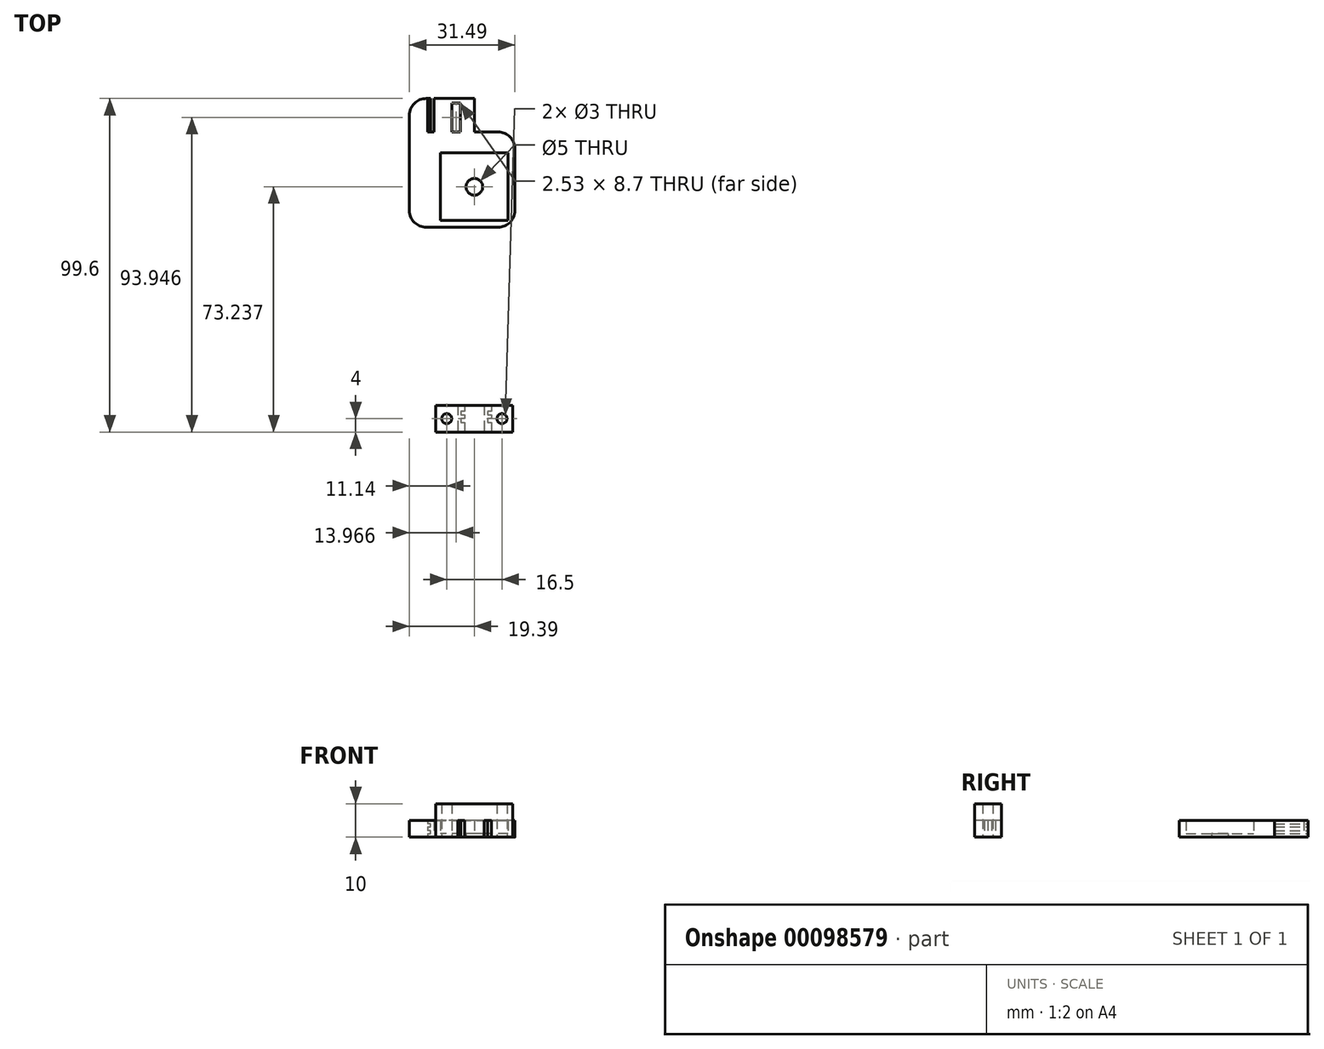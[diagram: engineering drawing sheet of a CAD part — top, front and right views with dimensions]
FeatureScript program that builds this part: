
annotation { "Feature Type Name" : "Feature", "Feature Type Description" : "" }
export const myFeature = defineFeature(function(context is Context, id is Id, definition is map)
    precondition{}
    {
        {
            var Q0;
            Q0=qCreatedBy(makeId("Top.planeOp"),FACE);
            var sketch = newSketch(context, id + "F0", { "sketchPlane" : qUnion([Q0])});
            skLineSegment(sketch, "E0.bottom", {"start": v(-11.5, 4) * mm, "end": v(11.5, 4) * mm});
            skLineSegment(sketch, "E0.top", {"start": v(-11.5, -4) * mm, "end": v(11.5, -4) * mm});
            skLineSegment(sketch, "E0.left", {"start": v(-11.5, 4) * mm, "end": v(-11.5, -4) * mm});
            skLineSegment(sketch, "E0.right", {"start": v(11.5, 4) * mm, "end": v(11.5, -4) * mm});
            skPoint(sketch, "E0.middle", {"position": v(0, 0) * mm});
            skLineSegment(sketch, "E1", {"start": v(-5, 4) * mm, "end": v(-5, -4) * mm});
            skLineSegment(sketch, "E2", {"start": v(-2.9, 4) * mm, "end": v(-2.9, 2.2) * mm});
            skLineSegment(sketch, "E3", {"start": v(-2.9, 2.2) * mm, "end": v(-4, 2.2) * mm});
            skLineSegment(sketch, "E4", {"start": v(-4, 2.2) * mm, "end": v(-4, 1.1) * mm});
            skLineSegment(sketch, "E5", {"start": v(-4, 1.1) * mm, "end": v(-2.9, 1.1) * mm});
            skLineSegment(sketch, "E6", {"start": v(-2.9, 1.1) * mm, "end": v(-2.9, 0) * mm});
            skLineSegment(sketch, "E7", {"start": v(-2.9, 0) * mm, "end": v(-4, 0) * mm});
            skLineSegment(sketch, "E8", {"start": v(-4, 0) * mm, "end": v(-4, -1.1) * mm});
            skLineSegment(sketch, "E9", {"start": v(-4, -1.1) * mm, "end": v(-2.9, -1.1) * mm});
            skLineSegment(sketch, "E10", {"start": v(-2.9, -1.1) * mm, "end": v(-2.9, -4) * mm});
            skLineSegment(sketch, "E11.1.0.0", {"start": v(5.1, 4) * mm, "end": v(5.1, 2.2) * mm});
            skLineSegment(sketch, "E11.1.0.1", {"start": v(5.1, 2.2) * mm, "end": v(4, 2.2) * mm});
            skLineSegment(sketch, "E11.1.0.2", {"start": v(4, 2.2) * mm, "end": v(4, 1.1) * mm});
            skLineSegment(sketch, "E11.1.0.3", {"start": v(4, 1.1) * mm, "end": v(5.1, 1.1) * mm});
            skLineSegment(sketch, "E11.1.0.4", {"start": v(5.1, 1.1) * mm, "end": v(5.1, 0) * mm});
            skLineSegment(sketch, "E11.1.0.5", {"start": v(5.1, 0) * mm, "end": v(4, 0) * mm});
            skLineSegment(sketch, "E11.1.0.6", {"start": v(4, 0) * mm, "end": v(4, -1.1) * mm});
            skLineSegment(sketch, "E11.1.0.7", {"start": v(4, -1.1) * mm, "end": v(5.1, -1.1) * mm});
            skLineSegment(sketch, "E11.1.0.8", {"start": v(5.1, -1.1) * mm, "end": v(5.1, -4) * mm});
            skLineSegment(sketch, "E11.1.0.9", {"start": v(3, 4) * mm, "end": v(3, -4) * mm});
            skLineSegment(sketch, "E11.direction1", {"start": v(-2.9, 2.2) * mm, "end": v(5.1, 2.2) * mm, "construction": true});
            skCircle(sketch, "E12", {"center": v(-8.25, 0) * mm, "radius": 1.5 * mm});
            skLineSegment(sketch, "E13", {"start": v(0, 4) * mm, "end": v(0, -4) * mm, "construction": true});
            skCircle(sketch, "E14.MirrorC", {"center": v(8.25, 0) * mm, "radius": 1.5 * mm});
            skSolve(sketch);
        }
        {
            var Q0;
            {var subQ1=sQuery(id+"F0.wireOp",EDGE,"E0.left");Q0=makeQuery(id+"F0.imprint","IMPRINT",FACE,{"disambiguationData":[TD([[makeQuery(id+"F0.imprint","IMPRINT",EDGE,{"derivedFrom":subQ1}),1.0]])]});}
            var Q1;
            {var subQ0=sQuery(id+"F0.wireOp",EDGE,"E1");Q1=makeQuery(id+"F0.imprint","IMPRINT",FACE,{"disambiguationData":[TD([[makeQuery(id+"F0.imprint","IMPRINT",EDGE,{"derivedFrom":subQ0}),1.0]])]});}
            var Q2;
            {var subQ1=sQuery(id+"F0.wireOp",EDGE,"E11.1.0.0");Q2=makeQuery(id+"F0.imprint","IMPRINT",FACE,{"disambiguationData":[TD([[makeQuery(id+"F0.imprint","IMPRINT",EDGE,{"derivedFrom":subQ1}),-1.0]])]});}
            var Q3;
            {var subQ0=sQuery(id+"F0.wireOp",EDGE,"E0.right");Q3=makeQuery(id+"F0.imprint","IMPRINT",FACE,{"disambiguationData":[TD([[makeQuery(id+"F0.imprint","IMPRINT",EDGE,{"derivedFrom":subQ0}),-1.0]])]});}
            var Q4;
            {var subQ0=sQuery(id+"F0.wireOp",EDGE,"E2");Q4=makeQuery(id+"F0.imprint","IMPRINT",FACE,{"disambiguationData":[TD([[makeQuery(id+"F0.imprint","IMPRINT",EDGE,{"derivedFrom":subQ0}),1.0]])]});}
            extrude(context, id + "F1", {"entities" : qUnion([Q0, Q1, Q2, Q3, Q4]), "depth" : 10 * mm});
        }
        {
            var Q0;
            {var subQ0=sQuery(id+"F0.wireOp",EDGE,"E1");Q0=makeQuery(id+"F0.imprint","IMPRINT",FACE,{"disambiguationData":[TD([[makeQuery(id+"F0.imprint","IMPRINT",EDGE,{"derivedFrom":subQ0}),1.0]])]});}
            var Q1;
            {var subQ1=sQuery(id+"F0.wireOp",EDGE,"E11.1.0.0");Q1=makeQuery(id+"F0.imprint","IMPRINT",FACE,{"disambiguationData":[TD([[makeQuery(id+"F0.imprint","IMPRINT",EDGE,{"derivedFrom":subQ1}),-1.0]])]});}
            extrude(context, id + "F2", {"entities" : qUnion([Q0, Q1]), "operationType" : NewBodyOperationType.REMOVE, "depth" : 5 * mm});
        }
        {
            var Q0;
            Q0=qCreatedBy(makeId("Top.planeOp"),FACE);
            var sketch = newSketch(context, id + "F3", { "sketchPlane" : qUnion([Q0])});
            skLineSegment(sketch, "E15.top", {"start": v(0, 95.6) * mm, "end": v(-12.1, 95.6) * mm});
            skLineSegment(sketch, "E15.left", {"start": v(12.1, 57.14) * mm, "end": v(12.1, 85.6) * mm});
            skLineSegment(sketch, "E15.right", {"start": v(-12.1, 85.6) * mm, "end": v(-12.1, 95.6) * mm});
            skPoint(sketch, "E15.middle", {"position": v(0, 69.24) * mm});
            skLineSegment(sketch, "E16.bottom", {"start": v(10.1, 59.14) * mm, "end": v(-10.1, 59.14) * mm});
            skLineSegment(sketch, "E16.top", {"start": v(10.1, 79.34) * mm, "end": v(-10.1, 79.34) * mm});
            skLineSegment(sketch, "E16.left", {"start": v(10.1, 59.14) * mm, "end": v(10.1, 79.34) * mm});
            skLineSegment(sketch, "E16.right", {"start": v(-10.1, 59.14) * mm, "end": v(-10.1, 79.34) * mm});
            skLineSegment(sketch, "E17", {"start": v(-12.1, 57.14) * mm, "end": v(12.1, 57.14) * mm});
            skCircle(sketch, "E18", {"center": v(0, 69.24) * mm, "radius": 2.5 * mm});
            skLineSegment(sketch, "E19", {"start": v(12.1, 85.6) * mm, "end": v(0, 85.6) * mm});
            skLineSegment(sketch, "E20", {"start": v(0, 85.6) * mm, "end": v(0, 95.6) * mm});
            skLineSegment(sketch, "E21", {"start": v(-12.1, 85.6) * mm, "end": v(-13.9, 85.6) * mm});
            skLineSegment(sketch, "E22", {"start": v(-13.9, 85.6) * mm, "end": v(-13.9, 95.6) * mm});
            skLineSegment(sketch, "E23", {"start": v(-13.9, 95.6) * mm, "end": v(-19.39, 95.6) * mm});
            skLineSegment(sketch, "E24", {"start": v(-19.39, 95.6) * mm, "end": v(-19.39, 57.14) * mm});
            skLineSegment(sketch, "E25", {"start": v(-19.39, 57.14) * mm, "end": v(-12.1, 57.14) * mm});
            skPoint(sketch, "E15.bottom.end.orphan", {"position": v(-12.1, 42.87) * mm});
            skPoint(sketch, "E26.orphan", {"position": v(12.1, 42.87) * mm});
            skPoint(sketch, "E27.orphan", {"position": v(12.1, 95.6) * mm});
            skLineSegment(sketch, "E28.bottom", {"start": v(-6.69, 85.6) * mm, "end": v(-4.16, 85.6) * mm});
            skLineSegment(sketch, "E28.top", {"start": v(-6.69, 94.3) * mm, "end": v(-4.16, 94.3) * mm});
            skLineSegment(sketch, "E28.left", {"start": v(-6.69, 85.6) * mm, "end": v(-6.69, 94.3) * mm});
            skLineSegment(sketch, "E28.right", {"start": v(-4.16, 85.6) * mm, "end": v(-4.16, 94.3) * mm});
            skSolve(sketch);
        }
        {
            var Q0;
            Q0=makeQuery(id+"F3.imprint","IMPRINT",FACE,{"disambiguationData":[TD([[makeQuery(id+"F3.imprint","IMPRINT",EDGE,{"derivedFrom":sQuery(id+"F3.wireOp",EDGE,"E15.top")}),1.0]])]});
            extrude(context, id + "F4", {"entities" : qUnion([Q0]), "depth" : 5 * mm});
        }
        {
            var Q0;
            Q0=makeQuery(id+"F3.imprint","IMPRINT",FACE,{"disambiguationData":[TD([[makeQuery(id+"F3.imprint","IMPRINT",EDGE,{"derivedFrom":sQuery(id+"F3.wireOp",EDGE,"E16.bottom")}),-1.0]])]});
            extrude(context, id + "F5", {"entities" : qUnion([Q0]), "operationType" : NewBodyOperationType.ADD, "depth" : 1 * mm});
        }
        {
            var Q0;
            Q0=makeQuery(id+"F4.opExtrude","SWEPT_FACE",FACE,{"disambiguationData":[OSD([sQuery(id+"F3.wireOp",EDGE,"E23")])]});
            var sketch = newSketch(context, id + "F6", { "sketchPlane" : qUnion([Q0])});
            skLineSegment(sketch, "E29", {"start": v(13.9, 3.99) * mm, "end": v(13, 3.99) * mm});
            skLineSegment(sketch, "E30", {"start": v(13, 3.99) * mm, "end": v(13, 3.09) * mm});
            skLineSegment(sketch, "E31", {"start": v(13, 3.09) * mm, "end": v(13.9, 3.09) * mm});
            skLineSegment(sketch, "E32.0.1.0", {"start": v(13, 1.06) * mm, "end": v(13.9, 1.06) * mm});
            skLineSegment(sketch, "E32.0.1.1", {"start": v(13, 1.96) * mm, "end": v(13, 1.06) * mm});
            skLineSegment(sketch, "E32.0.1.2", {"start": v(13.9, 1.96) * mm, "end": v(13, 1.96) * mm});
            skLineSegment(sketch, "E32.direction1", {"start": v(13, 3.09) * mm, "end": v(38, 3.09) * mm, "construction": true});
            skLineSegment(sketch, "E32.direction2", {"start": v(13, 3.09) * mm, "end": v(13, 1.06) * mm, "construction": true});
            skSolve(sketch);
        }
        {
            var Q0;
            {var subQ0=sQuery(id+"F6.wireOp",EDGE,"E29");Q0=makeQuery(id+"F6.imprint","IMPRINT",FACE,{"disambiguationData":[TD([[makeQuery(id+"F6.imprint","IMPRINT",EDGE,{"derivedFrom":subQ0}),1.0]])]});}
            var Q1;
            {var subQ0=sQuery(id+"F6.wireOp",EDGE,"E32.0.1.0");Q1=makeQuery(id+"F6.imprint","IMPRINT",FACE,{"disambiguationData":[TD([[makeQuery(id+"F6.imprint","IMPRINT",EDGE,{"derivedFrom":subQ0}),1.0]])]});}
            extrude(context, id + "F7", {"entities" : qUnion([Q0, Q1]), "operationType" : NewBodyOperationType.ADD, "oppositeDirection" : true, "depth" : 12 * mm});
        }
        {
            var Q0;
            Q0=makeQuery(id+"F4.opExtrude","SWEPT_EDGE",EDGE,{"disambiguationData":[OSD([sQuery(id+"F3.wireOp",EDGE,"E24"),sQuery(id+"F3.wireOp",EDGE,"E25")])]});
            var Q1;
            Q1=makeQuery(id+"F4.opExtrude","SWEPT_EDGE",EDGE,{"disambiguationData":[OSD([sQuery(id+"F3.wireOp",EDGE,"E15.left"),sQuery(id+"F3.wireOp",EDGE,"E17")])]});
            var Q2;
            Q2=makeQuery(id+"F4.opExtrude","SWEPT_EDGE",EDGE,{"disambiguationData":[OSD([sQuery(id+"F3.wireOp",EDGE,"E15.left"),sQuery(id+"F3.wireOp",EDGE,"E19")])]});
            var Q3;
            Q3=makeQuery(id+"F4.opExtrude","SWEPT_EDGE",EDGE,{"disambiguationData":[OSD([sQuery(id+"F3.wireOp",EDGE,"E23"),sQuery(id+"F3.wireOp",EDGE,"E24")])]});
            fillet(context, id + "F8", {"entities" : qUnion([Q0, Q1, Q2, Q3]), "radius" : 5 * mm, "tangentPropagation" : true, "allowEdgeOverflow" : false});
        }
    });
